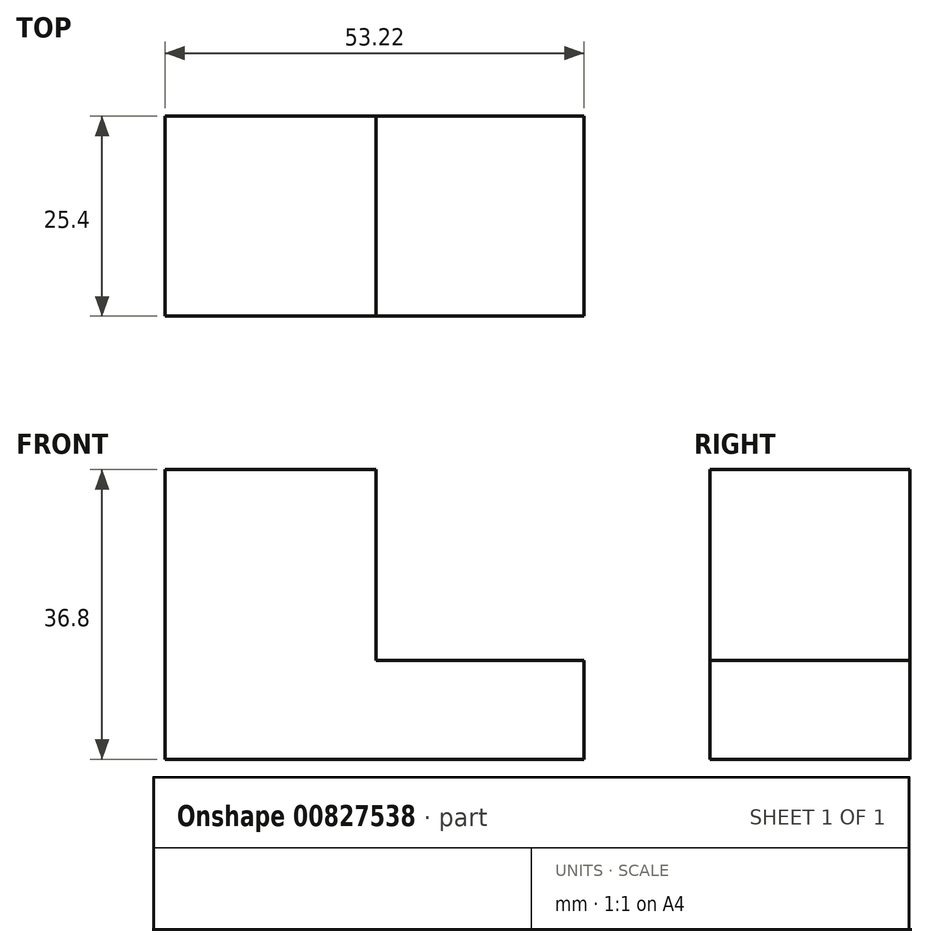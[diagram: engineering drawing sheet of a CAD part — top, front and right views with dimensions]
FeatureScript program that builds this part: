
annotation { "Feature Type Name" : "Feature", "Feature Type Description" : "" }
export const myFeature = defineFeature(function(context is Context, id is Id, definition is map)
    precondition{}
    {
        {
            var Q0;
            Q0=qCreatedBy(makeId("Front.planeOp"),FACE);
            var sketch = newSketch(context, id + "F0", { "sketchPlane" : qUnion([Q0])});
            skLineSegment(sketch, "E0.bottom", {"start": v(-70.67, 54.15) * mm, "end": v(-17.45, 54.15) * mm});
            skLineSegment(sketch, "E0.top", {"start": v(-70.67, 17.35) * mm, "end": v(-17.45, 17.35) * mm});
            skLineSegment(sketch, "E0.left", {"start": v(-70.67, 54.15) * mm, "end": v(-70.67, 17.35) * mm});
            skLineSegment(sketch, "E0.right", {"start": v(-17.45, 54.15) * mm, "end": v(-17.45, 17.35) * mm});
            skLineSegment(sketch, "E1.bottom", {"start": v(-43.89, 61.88) * mm, "end": v(6.52, 61.88) * mm});
            skLineSegment(sketch, "E1.top", {"start": v(-43.89, 29.9) * mm, "end": v(6.52, 29.9) * mm});
            skLineSegment(sketch, "E1.left", {"start": v(-43.89, 61.88) * mm, "end": v(-43.89, 29.9) * mm});
            skLineSegment(sketch, "E1.right", {"start": v(6.52, 61.88) * mm, "end": v(6.52, 29.9) * mm});
            skSolve(sketch);
        }
        {
            var Q0;
            {var subQ1=sQuery(id+"F0.wireOp",EDGE,"E0.top");Q0=makeQuery(id+"F0.imprint","IMPRINT",FACE,{"disambiguationData":[TD([[makeQuery(id+"F0.imprint","IMPRINT",EDGE,{"derivedFrom":subQ1}),1.0]])]});}
            extrude(context, id + "F1", {"entities" : qUnion([Q0]), "depth" : 25.4 * mm, "offsetDistance" : 25.4 * mm});
        }
    });
